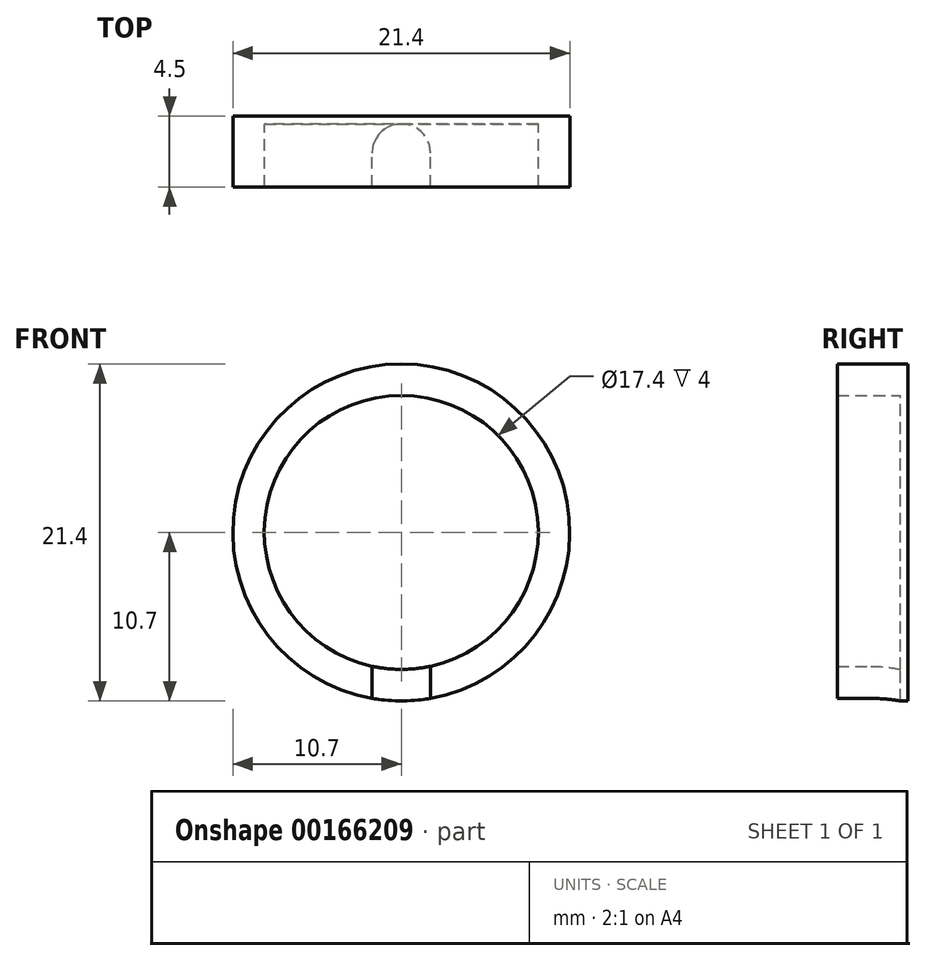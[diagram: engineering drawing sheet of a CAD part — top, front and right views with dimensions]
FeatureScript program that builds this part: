
annotation { "Feature Type Name" : "Feature", "Feature Type Description" : "" }
export const myFeature = defineFeature(function(context is Context, id is Id, definition is map)
    precondition{}
    {
        {
            assignVariable(context, id + "F0", {"name" : "Main_Length", "anyValue" : 4.5});
        }
        {
            assignVariable(context, id + "F1", {"name" : "Cap_Thickness", "anyValue" : 0.5});
        }
        {
            var Q0;
            Q0=qCreatedBy(makeId("Front.planeOp"),FACE);
            var sketch = newSketch(context, id + "F2", { "sketchPlane" : qUnion([Q0])});
            skCircle(sketch, "E0", {"center": v(0, 0) * mm, "radius": 10.7 * mm});
            skCircle(sketch, "E1", {"center": v(0, 0) * mm, "radius": 8.7 * mm});
            skSolve(sketch);
        }
        {
            var Q0;
            Q0=makeQuery(id+"F2.imprint","IMPRINT",FACE,{"disambiguationData":[TD([[makeQuery(id+"F2.imprint","IMPRINT",EDGE,{"derivedFrom":sQuery(id+"F2.wireOp",EDGE,"E0")}),1.0]])]});
            extrude(context, id + "F3", {"entities" : qUnion([Q0]), "depth" : (getVariable(context, 'Main_Length')) * mm});
        }
        {
            var Q0;
            Q0=qCreatedBy(makeId("Top.planeOp"),FACE);
            var sketch = newSketch(context, id + "F4", { "sketchPlane" : qUnion([Q0])});
            skArc(sketch, "E2", {"start": v(1.85, -2.35) * mm, "mid": v(0, -0.5) * mm, "end": v(-1.85, -2.35) * mm});
            skLineSegment(sketch, "E3", {"start": v(-1.85, -2.35) * mm, "end": v(-1.85, -4.5) * mm});
            skLineSegment(sketch, "E4", {"start": v(1.85, -2.35) * mm, "end": v(1.85, -4.5) * mm});
            skLineSegment(sketch, "E5.0", {"start": v(10.7, -4.5) * mm, "end": v(-10.7, -4.5) * mm});
            skSolve(sketch);
        }
        {
            var Q0;
            Q0=makeQuery(id+"F4.imprint","IMPRINT",FACE,{"disambiguationData":[TD([[makeQuery(id+"F4.imprint","IMPRINT",EDGE,{"derivedFrom":sQuery(id+"F4.wireOp",EDGE,"E2")}),1.0]])]});
            extrude(context, id + "F5", {"entities" : qUnion([Q0]), "operationType" : NewBodyOperationType.REMOVE, "endBound" : BoundingType.THROUGH_ALL, "oppositeDirection" : true, "depth" : 25 * mm});
        }
        {
            var Q0;
            Q0=makeQuery(id+"F2.imprint","IMPRINT",FACE,{"disambiguationData":[TD([[makeQuery(id+"F2.imprint","IMPRINT",EDGE,{"derivedFrom":sQuery(id+"F2.wireOp",EDGE,"E1")}),1.0]])]});
            extrude(context, id + "F6", {"entities" : qUnion([Q0]), "operationType" : NewBodyOperationType.ADD, "depth" : (getVariable(context, 'Cap_Thickness')) * mm});
        }
    });
